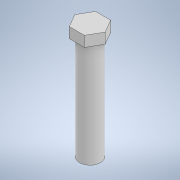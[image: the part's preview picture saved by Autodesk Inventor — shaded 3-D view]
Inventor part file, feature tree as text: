
AUTODESK INVENTOR PART (.ipt)
format: ipt  version: 2020.2 (Build 242310000, 310)  size: 104,448 bytes
history: native  units: in
note: dims shown in document units (in); Inventor stores cm internally (conversion verified against a paired STEP export)
features: extrude x2, sketch x2
ambient origin geometry x8: Origin, YZ Plane, XZ Plane, XY Plane, X Axis, Y Axis, Z Axis, Center Point
bodies: Solid1 (feature_tree)
feature tree (4):
  extrude  "Extrusion1"  Depth=0.3937in TaperAngle=0.0deg
  extrude  "Extrusion2"  Depth=0.0394in TaperAngle=0.0deg
  sketch  "Sketch1"  dims[d0=0.0787in d1=0.3937in d2=0.0in]
  sketch  "Sketch2"  dims[d3=0.0984in d4=0.0394in d5=0.0in]
